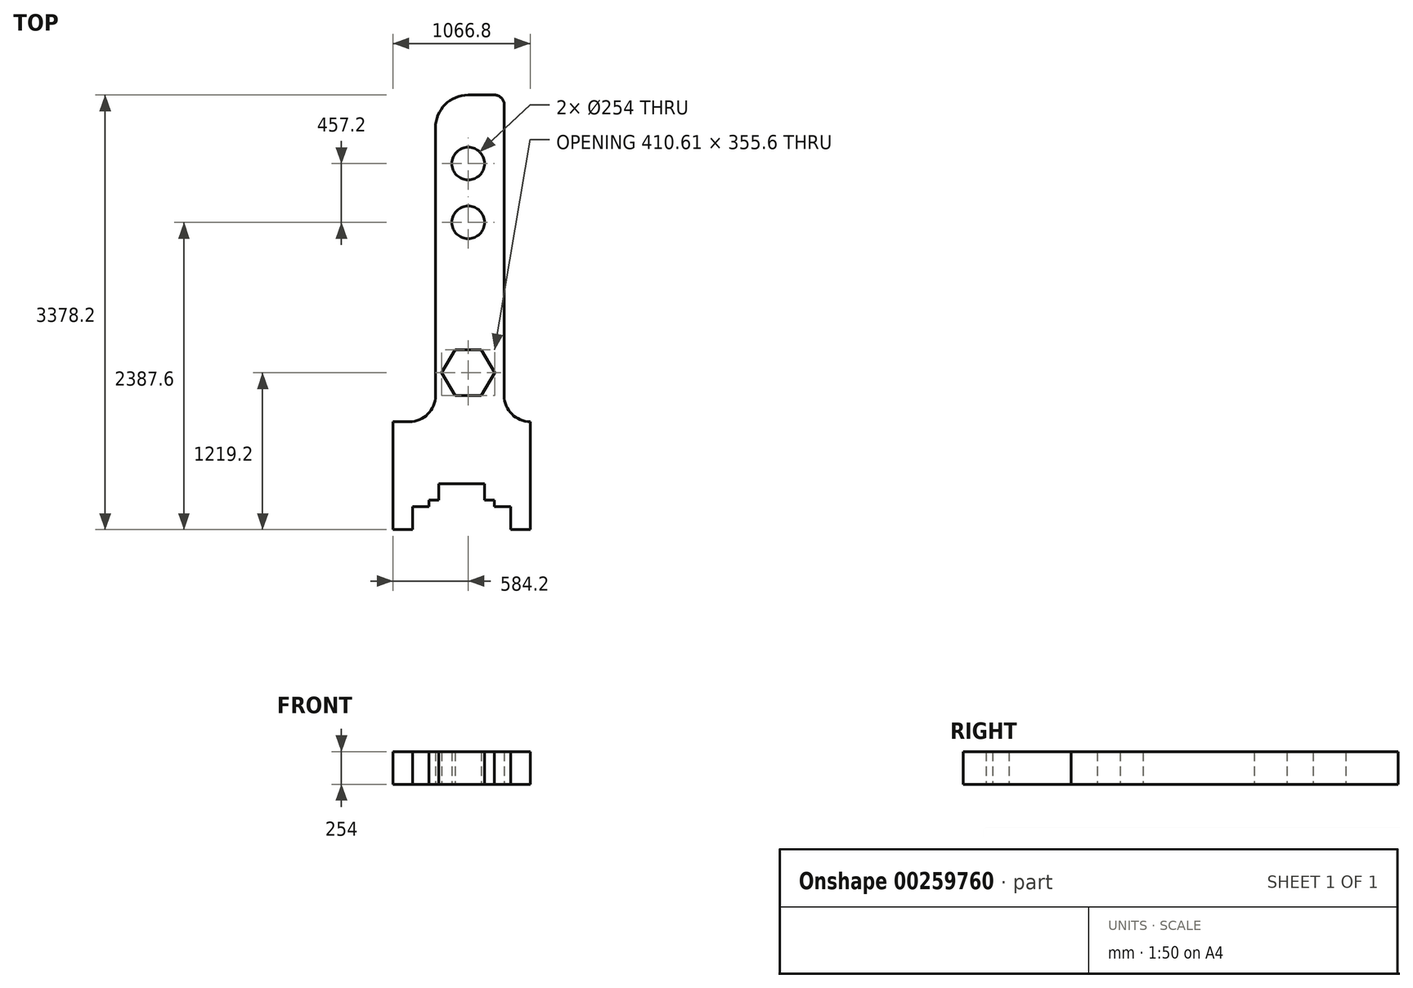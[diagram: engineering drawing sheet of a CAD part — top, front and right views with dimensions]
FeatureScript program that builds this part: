
annotation { "Feature Type Name" : "Feature", "Feature Type Description" : "" }
export const myFeature = defineFeature(function(context is Context, id is Id, definition is map)
    precondition{}
    {
        {
            var Q0;
            Q0=qCreatedBy(makeId("Top.planeOp"),FACE);
            var sketch = newSketch(context, id + "F0", { "sketchPlane" : qUnion([Q0])});
            skLineSegment(sketch, "E0", {"start": v(0, 0) * mm, "end": v(152.4, 0) * mm});
            skLineSegment(sketch, "E1", {"start": v(152.4, 0) * mm, "end": v(152.4, 177.8) * mm});
            skLineSegment(sketch, "E2", {"start": v(152.4, 177.8) * mm, "end": v(279.4, 177.8) * mm});
            skLineSegment(sketch, "E3", {"start": v(279.4, 177.8) * mm, "end": v(279.4, 228.6) * mm});
            skLineSegment(sketch, "E4", {"start": v(279.4, 228.6) * mm, "end": v(355.6, 228.6) * mm});
            skLineSegment(sketch, "E5", {"start": v(355.6, 228.6) * mm, "end": v(355.6, 355.6) * mm});
            skLineSegment(sketch, "E6", {"start": v(355.6, 355.6) * mm, "end": v(533.4, 355.6) * mm});
            skLineSegment(sketch, "E7", {"start": v(533.4, 355.6) * mm, "end": v(533.4, 322.8) * mm});
            skLineSegment(sketch, "E8.MirrorCS", {"start": v(711.2, 355.6) * mm, "end": v(533.4, 355.6) * mm});
            skLineSegment(sketch, "E9.MirrorCS", {"start": v(711.2, 228.6) * mm, "end": v(711.2, 355.6) * mm});
            skLineSegment(sketch, "E10.MirrorCS", {"start": v(787.4, 228.6) * mm, "end": v(711.2, 228.6) * mm});
            skLineSegment(sketch, "E11.MirrorCS", {"start": v(787.4, 177.8) * mm, "end": v(787.4, 228.6) * mm});
            skLineSegment(sketch, "E12.MirrorCS", {"start": v(914.4, 177.8) * mm, "end": v(787.4, 177.8) * mm});
            skLineSegment(sketch, "E13.MirrorCS", {"start": v(914.4, 0) * mm, "end": v(914.4, 177.8) * mm});
            skLineSegment(sketch, "E14.MirrorCS", {"start": v(1066.8, 0) * mm, "end": v(914.4, 0) * mm});
            skLineSegment(sketch, "E15", {"start": v(0, 0) * mm, "end": v(0, 838.2) * mm});
            skLineSegment(sketch, "E16", {"start": v(1066.8, 0) * mm, "end": v(1066.8, 838.2) * mm});
            skArc(sketch, "E17", {"start": v(863.6, 1041.4) * mm, "mid": v(923.12, 897.72) * mm, "end": v(1066.8, 838.2) * mm});
            skLineSegment(sketch, "E18", {"start": v(863.6, 1041.4) * mm, "end": v(863.6, 3302) * mm});
            skLineSegment(sketch, "E19", {"start": v(787.4, 3378.2) * mm, "end": v(584.2, 3378.2) * mm});
            skArc(sketch, "E20", {"start": v(584.2, 3378.2) * mm, "mid": v(404.6, 3303.8) * mm, "end": v(330.2, 3124.2) * mm});
            skLineSegment(sketch, "E21", {"start": v(330.2, 3124.2) * mm, "end": v(330.2, 1041.4) * mm});
            skArc(sketch, "E22", {"start": v(127, 838.2) * mm, "mid": v(270.68, 897.72) * mm, "end": v(330.2, 1041.4) * mm});
            skLineSegment(sketch, "E23", {"start": v(0, 838.2) * mm, "end": v(127, 838.2) * mm});
            skLineSegment(sketch, "E24", {"start": v(584.2, 3378.2) * mm, "end": v(584.2, 2971.8) * mm});
            skCircle(sketch, "E25.cCircle", {"center": v(584.2, 1219.2) * mm, "radius": 177.8 * mm, "construction": true});
            skLineSegment(sketch, "E25.0", {"start": v(686.85, 1041.4) * mm, "end": v(481.55, 1041.4) * mm});
            skLineSegment(sketch, "E25.1", {"start": v(481.55, 1041.4) * mm, "end": v(378.9, 1219.2) * mm});
            skLineSegment(sketch, "E25.2", {"start": v(378.9, 1219.2) * mm, "end": v(481.55, 1397) * mm});
            skLineSegment(sketch, "E25.3", {"start": v(481.55, 1397) * mm, "end": v(686.85, 1397) * mm});
            skLineSegment(sketch, "E25.4", {"start": v(686.85, 1397) * mm, "end": v(789.5, 1219.2) * mm});
            skLineSegment(sketch, "E25.5", {"start": v(789.5, 1219.2) * mm, "end": v(686.85, 1041.4) * mm});
            skPoint(sketch, "E25.0.midPoint", {"position": v(584.2, 1041.4) * mm});
            skCircle(sketch, "E26", {"center": v(584.2, 2387.6) * mm, "radius": 127 * mm});
            skLineSegment(sketch, "E27", {"start": v(584.2, 2387.6) * mm, "end": v(584.2, 2844.8) * mm});
            skCircle(sketch, "E28", {"center": v(584.2, 2844.8) * mm, "radius": 127 * mm});
            skLineSegment(sketch, "E29.trimOffspring", {"start": v(584.2, 2717.8) * mm, "end": v(584.2, 2387.6) * mm});
            skLineSegment(sketch, "E30.trimOffspring", {"start": v(584.2, 2844.8) * mm, "end": v(584.2, 1219.2) * mm});
            skArc(sketch, "E31", {"start": v(863.6, 3302) * mm, "mid": v(841.28, 3355.88) * mm, "end": v(787.4, 3378.2) * mm});
            skSolve(sketch);
        }
        {
            var Q0;
            Q0=makeQuery(id+"F0.imprint","IMPRINT",FACE,{"disambiguationData":[TD([[makeQuery(id+"F0.imprint","IMPRINT",EDGE,{"derivedFrom":sQuery(id+"F0.wireOp",EDGE,"E0")}),1.0]])]});
            extrude(context, id + "F1", {"entities" : qUnion([Q0]), "depth" : 254 * mm});
        }
    });
